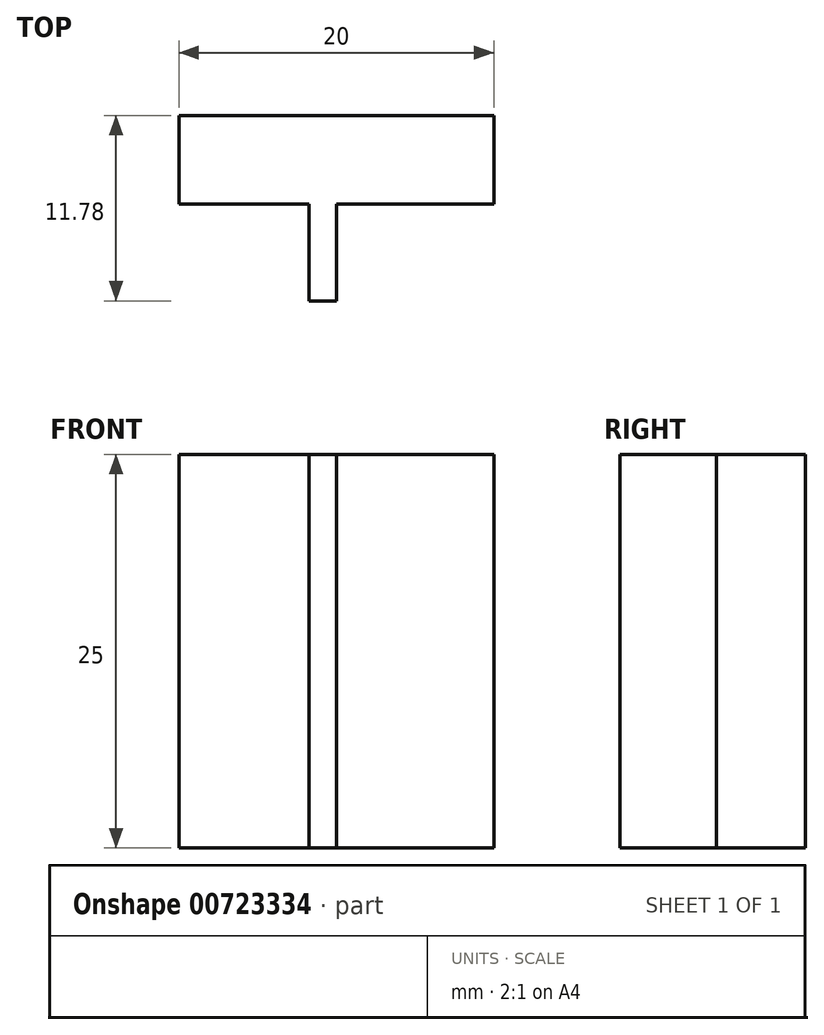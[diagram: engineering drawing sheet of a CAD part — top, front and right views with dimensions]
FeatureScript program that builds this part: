
annotation { "Feature Type Name" : "Feature", "Feature Type Description" : "" }
export const myFeature = defineFeature(function(context is Context, id is Id, definition is map)
    precondition{}
    {
        {
            var Q0;
            Q0=qCreatedBy(makeId("Top.planeOp"),FACE);
            var sketch = newSketch(context, id + "F0", { "sketchPlane" : qUnion([Q0])});
            skLineSegment(sketch, "E0.bottom", {"start": v(-2.19, 0) * mm, "end": v(-22.19, 0) * mm});
            skLineSegment(sketch, "E0.top", {"start": v(-2.19, 5.63) * mm, "end": v(-22.19, 5.63) * mm});
            skLineSegment(sketch, "E0.left", {"start": v(-2.19, 0) * mm, "end": v(-2.19, 5.63) * mm});
            skLineSegment(sketch, "E0.right", {"start": v(-22.19, 0) * mm, "end": v(-22.19, 5.63) * mm});
            skLineSegment(sketch, "E1.bottom", {"start": v(-13.94, 0) * mm, "end": v(-12.19, 0) * mm, "construction": true});
            skLineSegment(sketch, "E1.top", {"start": v(-13.94, -6.15) * mm, "end": v(-12.19, -6.15) * mm, "construction": true});
            skLineSegment(sketch, "E2.bottom", {"start": v(-13.94, 0) * mm, "end": v(-12.19, 0) * mm});
            skLineSegment(sketch, "E2.top", {"start": v(-13.94, -6.15) * mm, "end": v(-12.19, -6.15) * mm});
            skLineSegment(sketch, "E2.left", {"start": v(-13.94, 0) * mm, "end": v(-13.94, -6.15) * mm});
            skLineSegment(sketch, "E2.right", {"start": v(-12.19, 0) * mm, "end": v(-12.19, -6.15) * mm});
            skLineSegment(sketch, "E3.MirrorCS", {"start": v(-10.43, -6.15) * mm, "end": v(-12.19, -6.15) * mm, "construction": true});
            skLineSegment(sketch, "E4.MirrorCS", {"start": v(-10.43, 0) * mm, "end": v(-10.43, -6.15) * mm});
            skSolve(sketch);
        }
        {
            var Q0;
            Q0 = qSketchRegion(id + "F0", true);
            extrude(context, id + "F1", {"entities" : qUnion([Q0]), "depth" : 25 * mm, "offsetDistance" : 25 * mm});
        }
    });
